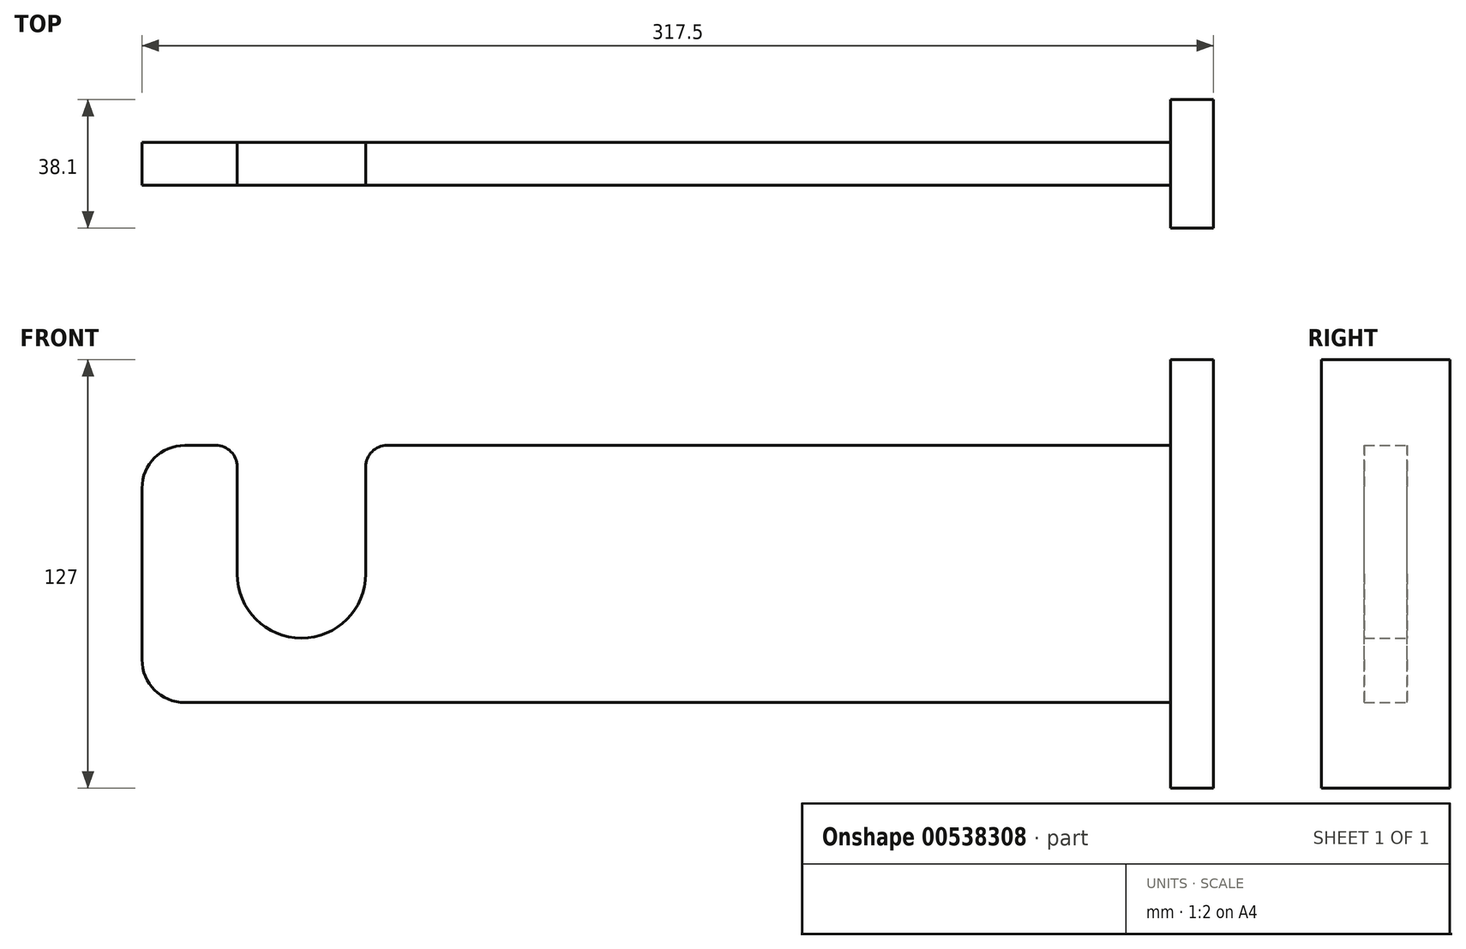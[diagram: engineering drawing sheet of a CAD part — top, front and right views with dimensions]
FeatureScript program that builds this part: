
annotation { "Feature Type Name" : "Feature", "Feature Type Description" : "" }
export const myFeature = defineFeature(function(context is Context, id is Id, definition is map)
    precondition{}
    {
        {
            var Q0;
            Q0=qCreatedBy(makeId("Front.planeOp"),FACE);
            var sketch = newSketch(context, id + "F0", { "sketchPlane" : qUnion([Q0])});
            skLineSegment(sketch, "E0", {"start": v(0, 216.14) * mm, "end": v(0, -230.8) * mm, "construction": true});
            skLineSegment(sketch, "E1", {"start": v(-208.82, 0) * mm, "end": v(213.21, 0) * mm, "construction": true});
            skLineSegment(sketch, "E2.bottom", {"start": v(152.4, -38.1) * mm, "end": v(-139.7, -38.1) * mm});
            skLineSegment(sketch, "E2.top", {"start": v(152.4, 38.1) * mm, "end": v(-79.75, 38.1) * mm});
            skLineSegment(sketch, "E2.left", {"start": v(152.4, -38.1) * mm, "end": v(152.4, 38.1) * mm});
            skLineSegment(sketch, "E2.right", {"start": v(-152.4, -25.4) * mm, "end": v(-152.4, 25.4) * mm});
            skPoint(sketch, "E2.middle", {"position": v(0, 0) * mm});
            skPoint(sketch, "E3.visualSharp", {"position": v(-152.4, 38.1) * mm});
            skArc(sketch, "E3.filletArc", {"start": v(-139.7, 38.1) * mm, "mid": v(-148.68, 34.38) * mm, "end": v(-152.4, 25.4) * mm});
            skPoint(sketch, "E4.visualSharp", {"position": v(-152.4, -38.1) * mm});
            skArc(sketch, "E4.filletArc", {"start": v(-152.4, -25.4) * mm, "mid": v(-148.68, -34.38) * mm, "end": v(-139.7, -38.1) * mm});
            skLineSegment(sketch, "E5", {"start": v(-124.2, 31.75) * mm, "end": v(-124.2, 0) * mm});
            skLineSegment(sketch, "E6", {"start": v(-124.2, 0) * mm, "end": v(-86.1, 0) * mm});
            skLineSegment(sketch, "E7", {"start": v(-86.1, 0) * mm, "end": v(-86.1, 31.75) * mm});
            skArc(sketch, "E8", {"start": v(-124.2, 0) * mm, "mid": v(-105.15, -19.05) * mm, "end": v(-86.1, 0) * mm});
            skLineSegment(sketch, "E9.trimOffspring", {"start": v(-130.55, 38.1) * mm, "end": v(-139.7, 38.1) * mm});
            skPoint(sketch, "E10.visualSharp", {"position": v(-86.1, 38.1) * mm});
            skArc(sketch, "E10.filletArc", {"start": v(-79.75, 38.1) * mm, "mid": v(-84.24, 36.24) * mm, "end": v(-86.1, 31.75) * mm});
            skPoint(sketch, "E11.visualSharp", {"position": v(-124.2, 38.1) * mm});
            skArc(sketch, "E11.filletArc", {"start": v(-124.2, 31.75) * mm, "mid": v(-126.06, 36.24) * mm, "end": v(-130.55, 38.1) * mm});
            skSolve(sketch);
        }
        {
            var Q0;
            Q0=makeQuery(id+"F0.imprint","IMPRINT",FACE,{"disambiguationData":[TD([[makeQuery(id+"F0.imprint","IMPRINT",EDGE,{"derivedFrom":sQuery(id+"F0.wireOp",EDGE,"E2.bottom")}),-1.0]])]});
            extrude(context, id + "F1", {"entities" : qUnion([Q0]), "depth" : 12.7 * mm, "offsetDistance" : 25.4 * mm});
        }
        {
            var Q0;
            Q0=makeQuery(id+"F1.opExtrude","SWEPT_FACE",FACE,{"disambiguationData":[OSD([sQuery(id+"F0.wireOp",EDGE,"E2.left")])]});
            var sketch = newSketch(context, id + "F2", { "sketchPlane" : qUnion([Q0])});
            skLineSegment(sketch, "E12.bottom", {"start": v(12.7, -63.5) * mm, "end": v(-25.4, -63.5) * mm});
            skLineSegment(sketch, "E12.top", {"start": v(12.7, 63.5) * mm, "end": v(-25.4, 63.5) * mm});
            skLineSegment(sketch, "E12.left", {"start": v(12.7, -63.5) * mm, "end": v(12.7, 63.5) * mm});
            skLineSegment(sketch, "E12.right", {"start": v(-25.4, -63.5) * mm, "end": v(-25.4, 63.5) * mm});
            skPoint(sketch, "E12.middle", {"position": v(-6.35, 0) * mm});
            skPoint(sketch, "E12.middle.positionSnap0", {"position": v(-6.35, 38.1) * mm});
            skPoint(sketch, "E12.centerSnap0", {"position": v(-6.35, 38.1) * mm});
            skSolve(sketch);
        }
        {
            var Q0;
            Q0 = qSketchRegion(id + "F2", true);
            extrude(context, id + "F3", {"entities" : qUnion([Q0]), "operationType" : NewBodyOperationType.ADD, "depth" : 12.7 * mm, "offsetDistance" : 25.4 * mm});
        }
    });
